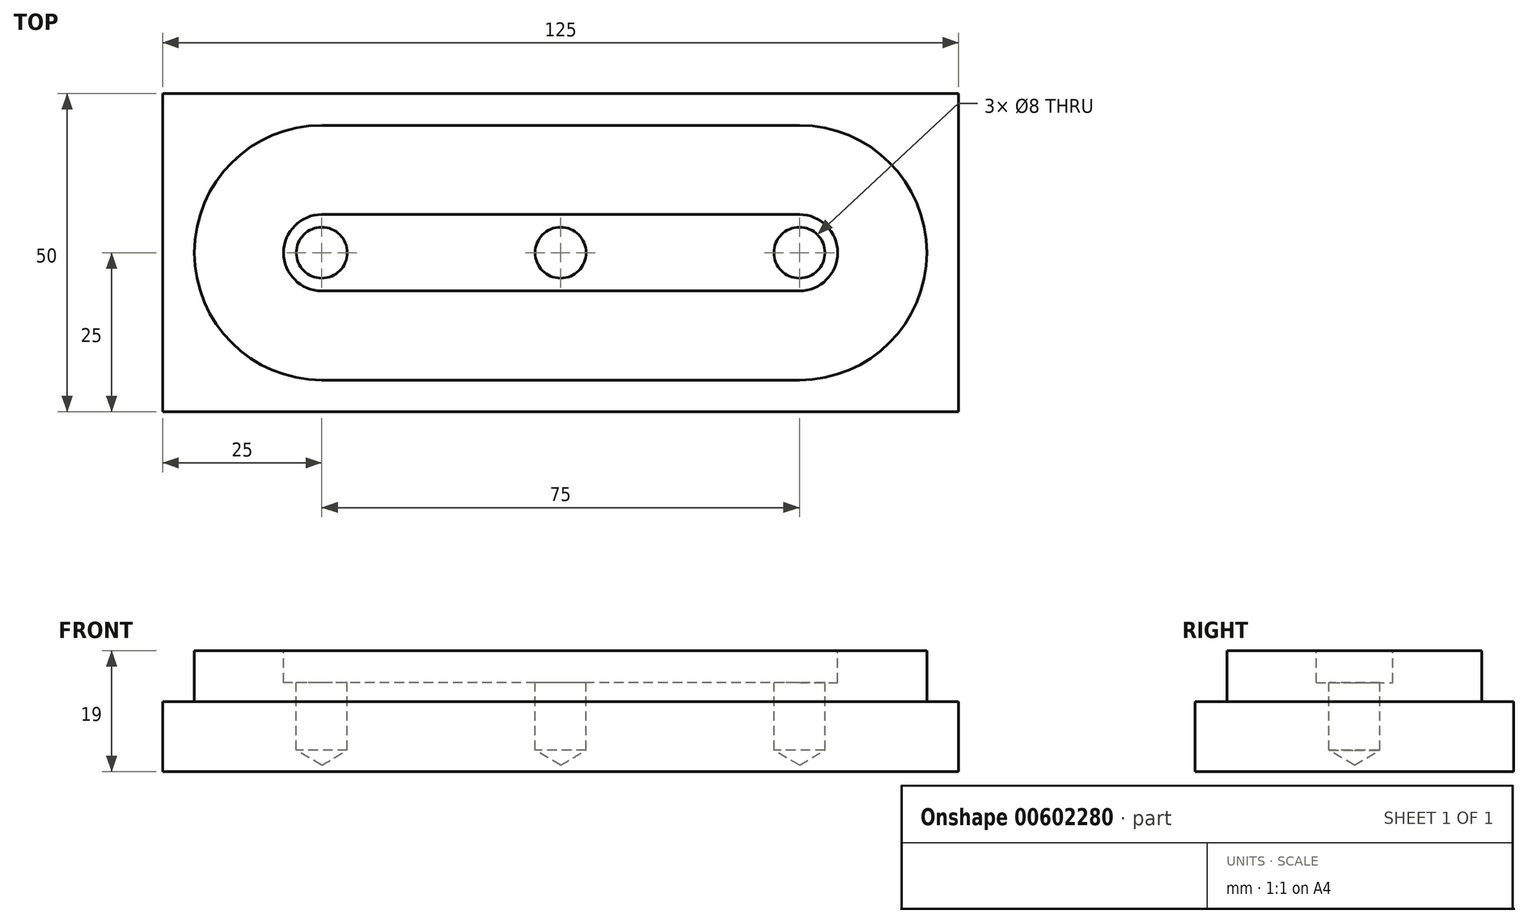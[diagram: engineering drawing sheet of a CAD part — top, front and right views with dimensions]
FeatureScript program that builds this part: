
annotation { "Feature Type Name" : "Feature", "Feature Type Description" : "" }
export const myFeature = defineFeature(function(context is Context, id is Id, definition is map)
    precondition{}
    {
        {
            var Q0;
            Q0=qCreatedBy(makeId("Top.planeOp"),FACE);
            var sketch = newSketch(context, id + "F0", { "sketchPlane" : qUnion([Q0])});
            skLineSegment(sketch, "E0.bottom", {"start": v(62.5, 25) * mm, "end": v(-62.5, 25) * mm});
            skLineSegment(sketch, "E0.top", {"start": v(62.5, -25) * mm, "end": v(-62.5, -25) * mm});
            skLineSegment(sketch, "E0.left", {"start": v(62.5, 25) * mm, "end": v(62.5, -25) * mm});
            skLineSegment(sketch, "E0.right", {"start": v(-62.5, 25) * mm, "end": v(-62.5, -25) * mm});
            skPoint(sketch, "E0.middle", {"position": v(0, 0) * mm});
            skSolve(sketch);
        }
        {
            var Q0;
            Q0=makeQuery(id+"F0.imprint","IMPRINT",FACE,{"disambiguationData":[TD([[makeQuery(id+"F0.imprint","IMPRINT",EDGE,{"derivedFrom":sQuery(id+"F0.wireOp",EDGE,"E0.bottom")}),1.0]])]});
            extrude(context, id + "F1", {"entities" : qUnion([Q0]), "depth" : 11 * mm, "offsetDistance" : 25 * mm});
        }
        {
            var Q0;
            Q0=makeQuery(id+"F1.opExtrude","CAP_FACE",FACE,{"disambiguationData":[OSD([sQuery(id+"F0.wireOp",EDGE,"E0.bottom"),sQuery(id+"F0.wireOp",EDGE,"E0.top"),sQuery(id+"F0.wireOp",EDGE,"E0.left"),sQuery(id+"F0.wireOp",EDGE,"E0.right")])],"isStart":false});
            var sketch = newSketch(context, id + "F2", { "sketchPlane" : qUnion([Q0])});
            skLineSegment(sketch, "E1.bottom", {"start": v(37.5, 20) * mm, "end": v(-37.5, 20) * mm});
            skLineSegment(sketch, "E1.top", {"start": v(37.5, -20) * mm, "end": v(-37.5, -20) * mm});
            skPoint(sketch, "E1.middle", {"position": v(0, 0) * mm});
            skArc(sketch, "E2", {"start": v(-37.5, 20) * mm, "mid": v(-57.5, 0) * mm, "end": v(-37.5, -20) * mm});
            skArc(sketch, "E3", {"start": v(37.5, -20) * mm, "mid": v(57.5, 0) * mm, "end": v(37.5, 20) * mm});
            skPoint(sketch, "E4.orphan", {"position": v(57.5, 20) * mm});
            skPoint(sketch, "E5.orphan", {"position": v(57.5, -20) * mm});
            skPoint(sketch, "E1.right.start.orphan", {"position": v(-57.5, 20) * mm});
            skPoint(sketch, "E6.orphan", {"position": v(-57.5, -20) * mm});
            skSolve(sketch);
        }
        {
            var Q0;
            Q0 = qSketchRegion(id + "F2", true);
            extrude(context, id + "F3", {"entities" : qUnion([Q0]), "operationType" : NewBodyOperationType.ADD, "depth" : 8 * mm, "offsetDistance" : 25 * mm});
        }
        {
            var Q0;
            Q0=makeQuery(id+"F3.opExtrude","CAP_FACE",FACE,{"disambiguationData":[OSD([sQuery(id+"F2.wireOp",EDGE,"E1.bottom"),sQuery(id+"F2.wireOp",EDGE,"E1.top"),sQuery(id+"F2.wireOp",EDGE,"E2"),sQuery(id+"F2.wireOp",EDGE,"E3")])],"isStart":false});
            var sketch = newSketch(context, id + "F4", { "sketchPlane" : qUnion([Q0])});
            skLineSegment(sketch, "E7.bottom", {"start": v(37.5, 6) * mm, "end": v(-37.5, 6) * mm});
            skLineSegment(sketch, "E7.top", {"start": v(37.5, -6) * mm, "end": v(-37.5, -6) * mm});
            skPoint(sketch, "E7.middle", {"position": v(0, 0) * mm});
            skArc(sketch, "E8", {"start": v(37.5, -6) * mm, "mid": v(43.5, 0) * mm, "end": v(37.5, 6) * mm});
            skArc(sketch, "E9", {"start": v(-37.5, 6) * mm, "mid": v(-43.5, 0) * mm, "end": v(-37.5, -6) * mm});
            skSolve(sketch);
        }
        {
            var Q0;
            Q0 = qSketchRegion(id + "F4", true);
            extrude(context, id + "F5", {"entities" : qUnion([Q0]), "operationType" : NewBodyOperationType.REMOVE, "oppositeDirection" : true, "depth" : 5 * mm, "offsetDistance" : 25 * mm});
        }
        {
            var Q0;
            Q0=makeQuery(id+"F5.boolean.opBoolean","COPY",FACE,{"derivedFrom":makeQuery(id+"F5.opExtrude","CAP_FACE",FACE,{"disambiguationData":[OSD([sQuery(id+"F4.wireOp",EDGE,"E7.bottom"),sQuery(id+"F4.wireOp",EDGE,"E7.top"),sQuery(id+"F4.wireOp",EDGE,"E8"),sQuery(id+"F4.wireOp",EDGE,"E9")])],"isStart":false})});
            var sketch = newSketch(context, id + "F6", { "sketchPlane" : qUnion([Q0])});
            skPoint(sketch, "E10", {"position": v(0, 0) * mm});
            skSolve(sketch);
        }
        {
            var Q0;
            Q0=sQuery(id+"F6.wireOp",VERTEX,"E10");
            var Q1;
            Q1=makeQuery(id+"F1.opExtrude","SWEPT_BODY",BODY,{"disambiguationData":[OSD([sQuery(id+"F0.wireOp",EDGE,"E0.bottom"),sQuery(id+"F0.wireOp",EDGE,"E0.top"),sQuery(id+"F0.wireOp",EDGE,"E0.left"),sQuery(id+"F0.wireOp",EDGE,"E0.right")])]});
            hole(context, id + "F7", {"style" : HoleStyle.SIMPLE, "endStyle" : HoleEndStyle.BLIND, "holeDiameter" : 8 * mm, "majorDiameter" : 5 * mm, "holeDepth" : 10.6 * mm, "isTappedThrough" : true, "tappedDepth" : 12 * mm, "tapClearance" : 3, "locations" : qUnion([Q0]), "scope" : qUnion([Q1])});
        }
        {
            var Q0;
            Q0=makeQuery(id+"F5.boolean.opBoolean","COPY",FACE,{"derivedFrom":makeQuery(id+"F5.opExtrude","CAP_FACE",FACE,{"disambiguationData":[OSD([sQuery(id+"F4.wireOp",EDGE,"E7.bottom"),sQuery(id+"F4.wireOp",EDGE,"E7.top"),sQuery(id+"F4.wireOp",EDGE,"E8"),sQuery(id+"F4.wireOp",EDGE,"E9")])],"isStart":false})});
            var sketch = newSketch(context, id + "F8", { "sketchPlane" : qUnion([Q0])});
            skPoint(sketch, "E11", {"position": v(-37.5, 0) * mm});
            skPoint(sketch, "E12", {"position": v(37.5, 0) * mm});
            skSolve(sketch);
        }
        {
            var Q0;
            Q0=sQuery(id+"F8.wireOp",VERTEX,"E11");
            var Q1;
            Q1=sQuery(id+"F8.wireOp",VERTEX,"E12");
            var Q2;
            Q2=makeQuery(id+"F1.opExtrude","SWEPT_BODY",BODY,{"disambiguationData":[OSD([sQuery(id+"F0.wireOp",EDGE,"E0.bottom"),sQuery(id+"F0.wireOp",EDGE,"E0.top"),sQuery(id+"F0.wireOp",EDGE,"E0.left"),sQuery(id+"F0.wireOp",EDGE,"E0.right")])]});
            hole(context, id + "F9", {"style" : HoleStyle.SIMPLE, "endStyle" : HoleEndStyle.BLIND, "holeDiameter" : 8 * mm, "majorDiameter" : 5 * mm, "holeDepth" : 10.6 * mm, "isTappedThrough" : true, "tappedDepth" : 12 * mm, "tapClearance" : 3, "locations" : qUnion([Q0, Q1]), "scope" : qUnion([Q2])});
        }
    });
